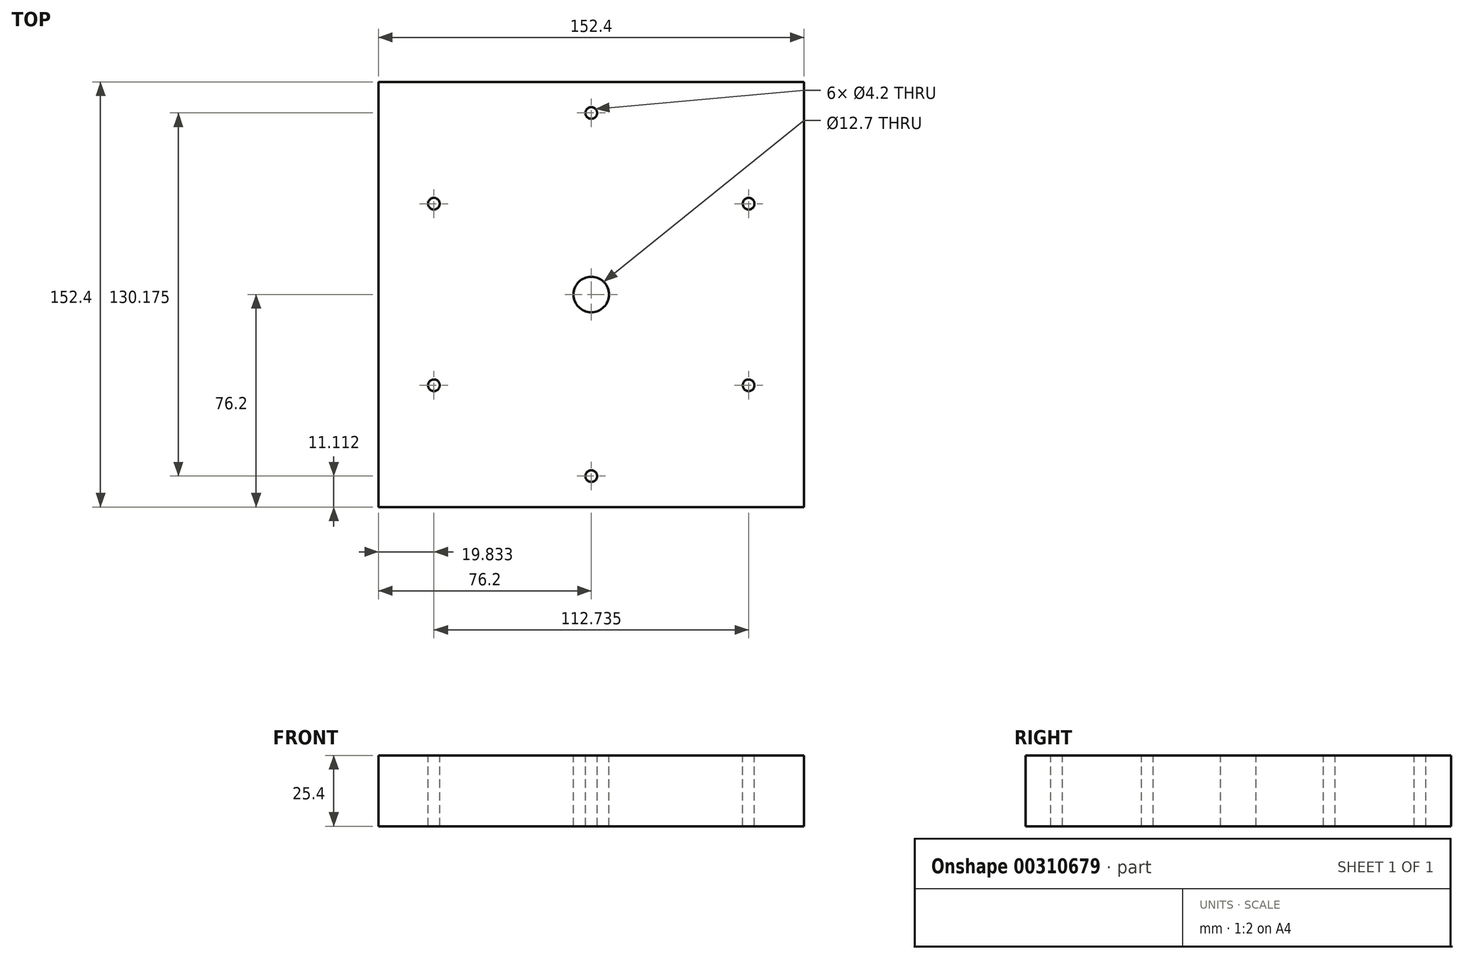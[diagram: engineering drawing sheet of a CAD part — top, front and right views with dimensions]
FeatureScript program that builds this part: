
annotation { "Feature Type Name" : "Feature", "Feature Type Description" : "" }
export const myFeature = defineFeature(function(context is Context, id is Id, definition is map)
    precondition{}
    {
        {
            var Q0;
            Q0=qCreatedBy(makeId("Top.planeOp"),FACE);
            var sketch = newSketch(context, id + "F0", { "sketchPlane" : qUnion([Q0])});
            skCircle(sketch, "E0", {"center": v(0, 0) * mm, "radius": 65.09 * mm, "construction": true});
            skPoint(sketch, "E1", {"position": v(0, 65.09) * mm});
            skPoint(sketch, "E2", {"position": v(0, -65.09) * mm});
            skPoint(sketch, "E3", {"position": v(-56.37, -32.54) * mm});
            skPoint(sketch, "E4", {"position": v(-56.37, 32.54) * mm});
            skPoint(sketch, "E5", {"position": v(56.37, 32.54) * mm});
            skPoint(sketch, "E6", {"position": v(56.37, -32.54) * mm});
            skLineSegment(sketch, "E7", {"start": v(0, 65.09) * mm, "end": v(56.37, 32.54) * mm, "construction": true});
            skLineSegment(sketch, "E8", {"start": v(56.37, -32.54) * mm, "end": v(56.37, 32.54) * mm, "construction": true});
            skLineSegment(sketch, "E9.bottom", {"start": v(-76.2, 76.2) * mm, "end": v(76.2, 76.2) * mm});
            skLineSegment(sketch, "E9.top", {"start": v(-76.2, -76.2) * mm, "end": v(76.2, -76.2) * mm});
            skLineSegment(sketch, "E9.left", {"start": v(-76.2, 76.2) * mm, "end": v(-76.2, -76.2) * mm});
            skLineSegment(sketch, "E9.right", {"start": v(76.2, 76.2) * mm, "end": v(76.2, -76.2) * mm});
            skLineSegment(sketch, "E10", {"start": v(-76.2, -76.2) * mm, "end": v(76.2, 76.2) * mm, "construction": true});
            skCircle(sketch, "E11", {"center": v(0, 0) * mm, "radius": 6.35 * mm});
            skSolve(sketch);
        }
        {
            var Q0;
            Q0 = qSketchRegion(id + "F0", true);
            extrude(context, id + "F1", {"entities" : qUnion([Q0]), "oppositeDirection" : true, "depth" : 25.4 * mm});
        }
        {
            var Q0;
            Q0=sQuery(id+"F0.wireOp",VERTEX,"E1");
            var Q1;
            Q1=sQuery(id+"F0.wireOp",VERTEX,"E4");
            var Q2;
            Q2=sQuery(id+"F0.wireOp",VERTEX,"E3");
            var Q3;
            Q3=sQuery(id+"F0.wireOp",VERTEX,"E2");
            var Q4;
            Q4=sQuery(id+"F0.wireOp",VERTEX,"E6");
            var Q5;
            Q5=sQuery(id+"F0.wireOp",VERTEX,"E5");
            var Q6;
            Q6=makeQuery(id+"F1.opExtrude","SWEPT_BODY",BODY,{"disambiguationData":[OSD([sQuery(id+"F0.wireOp",EDGE,"E9.bottom"),sQuery(id+"F0.wireOp",EDGE,"E9.top"),sQuery(id+"F0.wireOp",EDGE,"E9.left"),sQuery(id+"F0.wireOp",EDGE,"E9.right")])]});
            hole(context, id + "F2", {"style" : HoleStyle.SIMPLE, "endStyle" : HoleEndStyle.THROUGH, "standardTappedOrClearance" : lookupTablePath({ "standard" : "ISO", "engagement" : "75%", "pitch" : "0.8 mm", "size" : "M5", "type" : "Tapped" }), "standardBlindInLast" : lookupTablePath({ "standard" : "ISO", "engagement" : "75%", "pitch" : "0.8 mm", "size" : "M5", "type" : "Tapped" }), "holeDiameter" : 4.2 * mm, "showTappedDepth" : true, "tappedDepth" : 5 * mm, "tapClearance" : 3, "locations" : qUnion([Q0, Q1, Q2, Q3, Q4, Q5]), "scope" : qUnion([Q6]), "majorDiameter" : 5 * mm});
        }
    });
